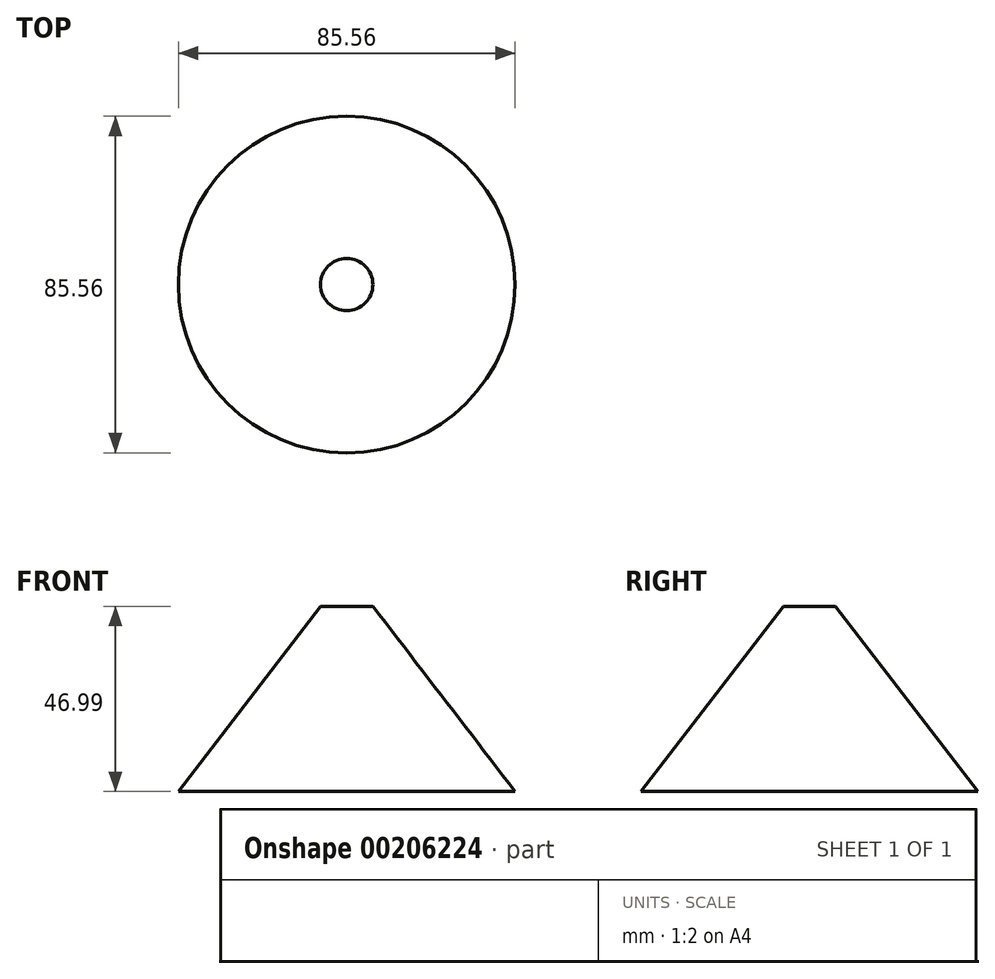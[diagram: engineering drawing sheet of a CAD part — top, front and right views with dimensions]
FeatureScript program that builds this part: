
annotation { "Feature Type Name" : "Feature", "Feature Type Description" : "" }
export const myFeature = defineFeature(function(context is Context, id is Id, definition is map)
    precondition{}
    {
        {
            var Q0;
            Q0=qCreatedBy(makeId("Front.planeOp"),FACE);
            var sketch = newSketch(context, id + "F0", { "sketchPlane" : qUnion([Q0])});
            skLineSegment(sketch, "E0", {"start": v(0, 46.99) * mm, "end": v(6.65, 46.99) * mm});
            skLineSegment(sketch, "E1", {"start": v(6.65, 46.99) * mm, "end": v(42.78, 0) * mm});
            skLineSegment(sketch, "E2", {"start": v(42.78, 0) * mm, "end": v(0, 0) * mm});
            skLineSegment(sketch, "E3", {"start": v(0, 0) * mm, "end": v(0, 46.99) * mm, "construction": true});
            skSolve(sketch);
        }
        {
            var Q0;
            Q0=sQuery(id+"F0.wireOp",EDGE,"E0");
            var Q1;
            Q1=sQuery(id+"F0.wireOp",EDGE,"E1");
            var Q2;
            Q2=sQuery(id+"F0.wireOp",EDGE,"E2");
            var Q3;
            Q3=sQuery(id+"F0.wireOp",EDGE,"E3");
            revolve(context, id + "F1", {"bodyType" : ToolBodyType.SURFACE, "surfaceEntities" : qUnion([Q0, Q1, Q2]), "axis" : qUnion([Q3]), "revolveType" : RevolveType.FULL});
        }
    });
